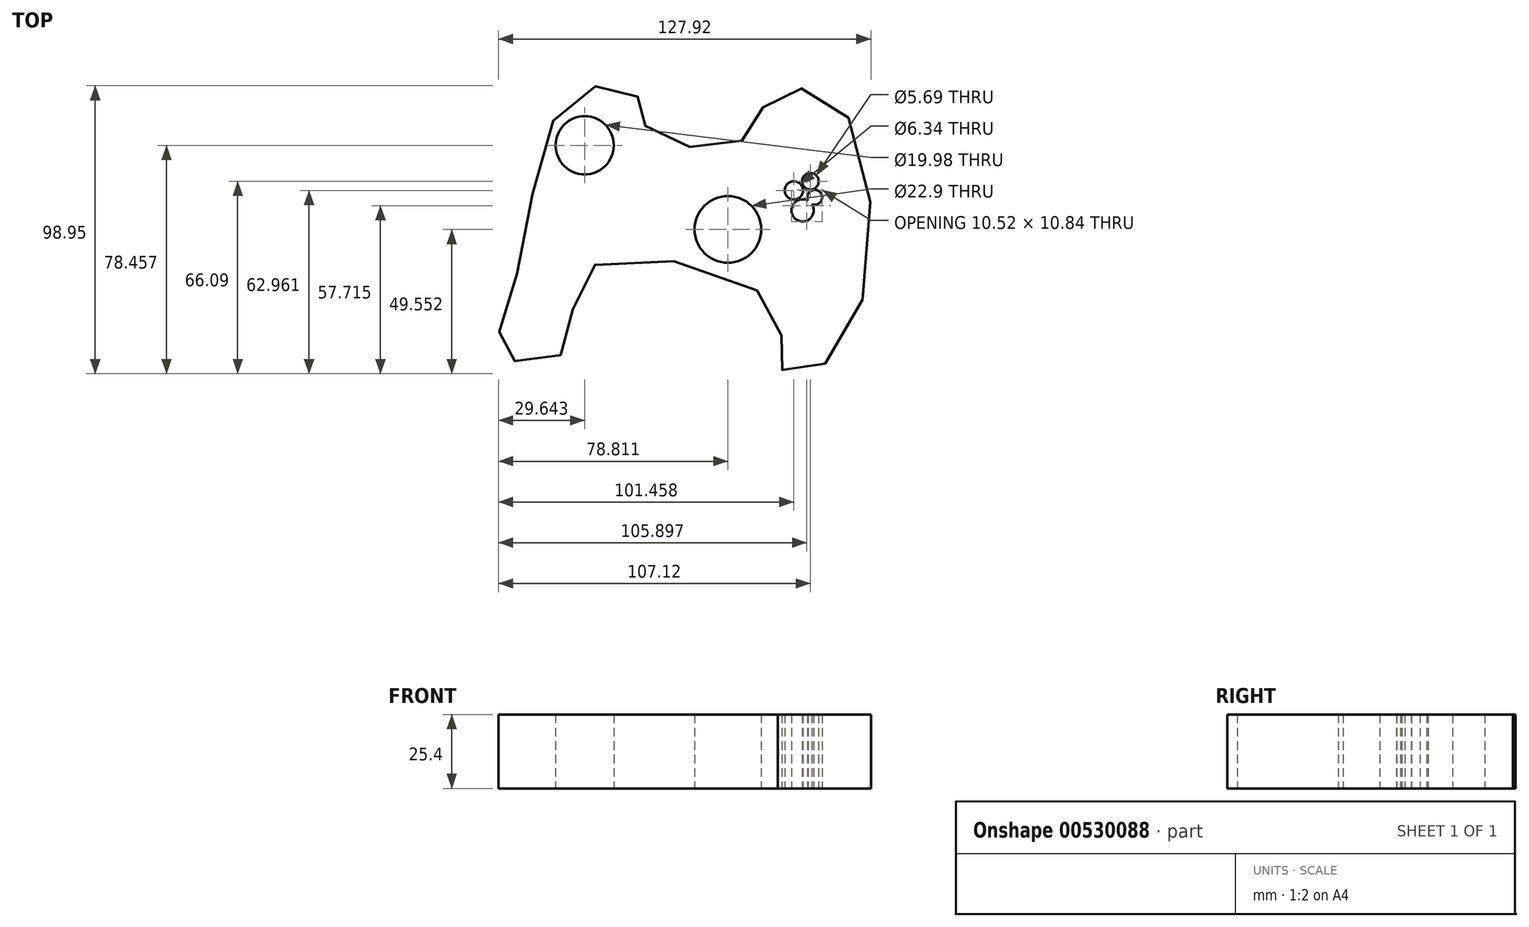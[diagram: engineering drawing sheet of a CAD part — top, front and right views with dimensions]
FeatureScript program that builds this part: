
annotation { "Feature Type Name" : "Feature", "Feature Type Description" : "" }
export const myFeature = defineFeature(function(context is Context, id is Id, definition is map)
    precondition{}
    {
        {
            var Q0;
            Q0=qCreatedBy(makeId("Top.planeOp"),FACE);
            var sketch = newSketch(context, id + "F0", { "sketchPlane" : qUnion([Q0])});
            skFitSpline(sketch, "E0", {"points": [v(-54.83, -31.74) * mm, v(-35.76, 29.35) * mm, v(-13.11, 28.76) * mm, v(-10.13, 18.03) * mm, v(20.86, 12.96) * mm, v(31.59, 27.86) * mm, v(56.32, 25.48) * mm, v(55.72, -58.26) * mm, v(35.16, -63.62) * mm, v(34.27, -43.66) * mm, v(-30.7, -30.25) * mm, v(-38.44, -58.26) * mm, v(-59.3, -59.75) * mm, v(-54.83, -31.74) * mm]});
            skCircle(sketch, "E1", {"center": v(17.58, -16.54) * mm, "radius": 11.45 * mm});
            skCircle(sketch, "E2", {"center": v(-31.59, 12.37) * mm, "radius": 10 * mm});
            skCircle(sketch, "E3", {"center": v(40.23, -3.13) * mm, "radius": 3.17 * mm});
            skCircle(sketch, "E4", {"center": v(45.9, 0) * mm, "radius": 2.85 * mm});
            skCircle(sketch, "E5", {"center": v(47.38, -5.51) * mm, "radius": 2.56 * mm});
            skCircle(sketch, "E6", {"center": v(43.2, -9.98) * mm, "radius": 3.82 * mm});
            skFitSpline(sketch, "E7", {"points": [v(-23.24, -11.17) * mm, v(-33.08, -12.07) * mm, v(-33.67, -12.07) * mm, v(-33.37, -16.54) * mm, v(-23.24, -16.84) * mm, v(-22.95, -23.4) * mm], "startDerivative": vector(-48.11, -6.6) * mm, "endDerivative": vector(-10.08, -39.88) * mm});
            skSolve(sketch);
        }
        {
            var Q0;
            Q0=makeQuery(id+"F0.imprint","IMPRINT",FACE,{"disambiguationData":[TD([[makeQuery(id+"F0.imprint","IMPRINT",EDGE,{"derivedFrom":sQuery(id+"F0.wireOp",EDGE,"E0")}),-1.0]])]});
            extrude(context, id + "F1", {"entities" : qUnion([Q0]), "depth" : 25.4 * mm, "offsetDistance" : 25.4 * mm});
        }
    });
